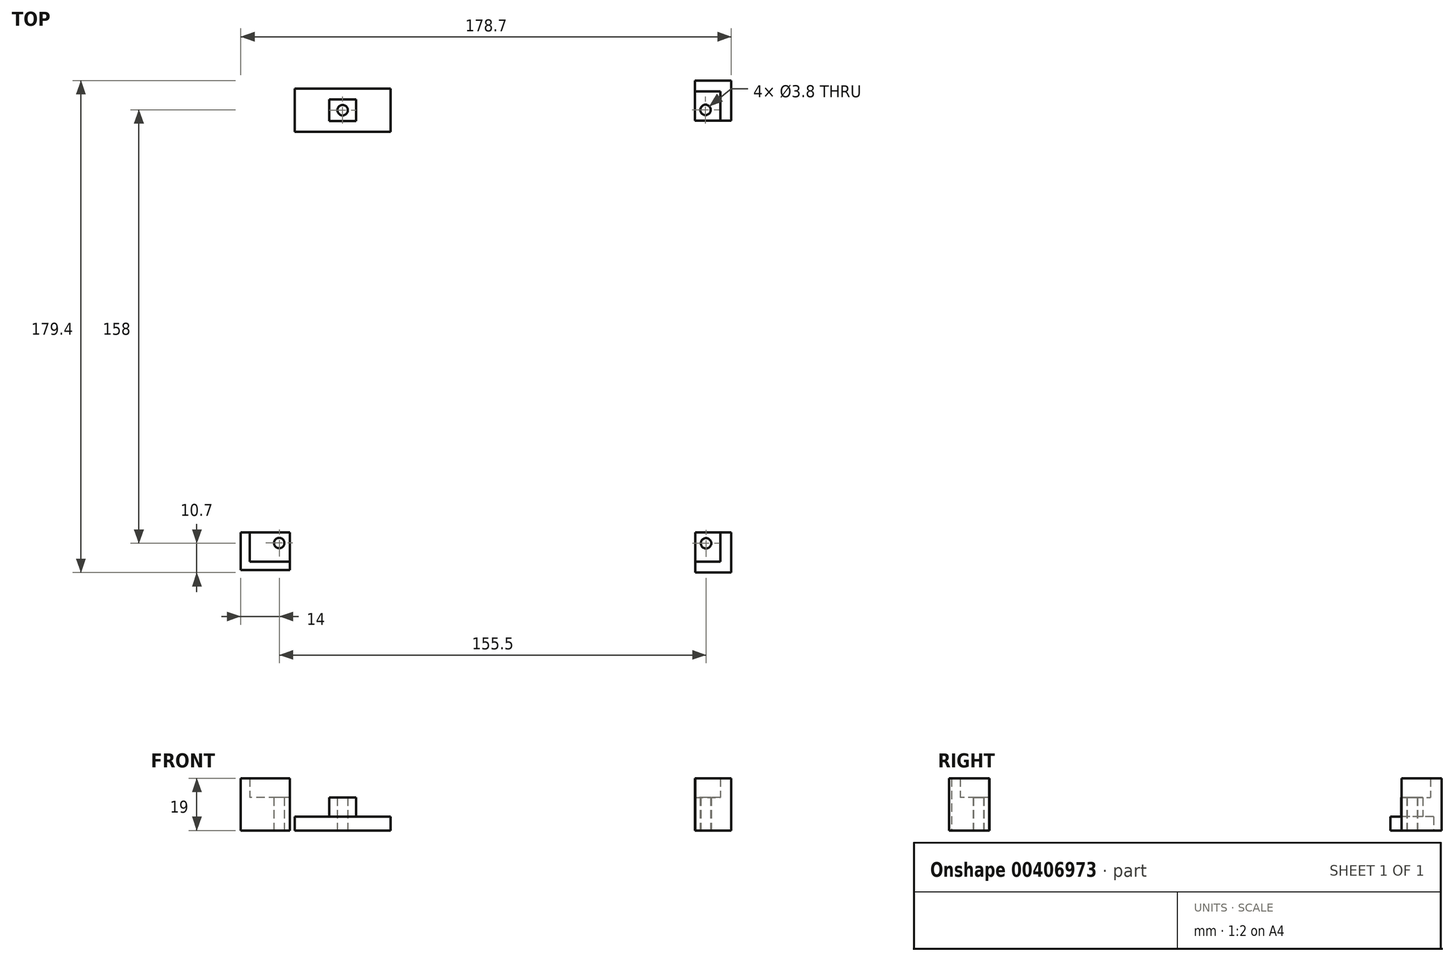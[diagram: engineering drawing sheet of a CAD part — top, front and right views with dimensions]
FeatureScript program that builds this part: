
annotation { "Feature Type Name" : "Feature", "Feature Type Description" : "" }
export const myFeature = defineFeature(function(context is Context, id is Id, definition is map)
    precondition{}
    {
        {
            var Q0;
            Q0=qCreatedBy(makeId("Top.planeOp"),FACE);
            var sketch = newSketch(context, id + "F0", { "sketchPlane" : qUnion([Q0])});
            skLineSegment(sketch, "E0.bottom", {"start": v(10, 10) * mm, "end": v(180, 10) * mm});
            skLineSegment(sketch, "E0.top", {"start": v(10, 180) * mm, "end": v(180, 180) * mm});
            skLineSegment(sketch, "E0.left", {"start": v(10, 10) * mm, "end": v(10, 180) * mm});
            skLineSegment(sketch, "E0.right", {"start": v(180, 10) * mm, "end": v(180, 180) * mm});
            skSolve(sketch);
        }
        {
            var Q0;
            Q0=qCreatedBy(makeId("Top.planeOp"),FACE);
            var sketch = newSketch(context, id + "F1", { "sketchPlane" : qUnion([Q0])});
            skCircle(sketch, "E1", {"center": v(175.5, 16) * mm, "radius": 1.5 * mm});
            skPoint(sketch, "E2", {"position": v(174, 16) * mm});
            skPoint(sketch, "E3", {"position": v(177, 16) * mm});
            skPoint(sketch, "E4", {"position": v(175.5, 14.5) * mm});
            skCircle(sketch, "E5", {"center": v(20, 16.1) * mm, "radius": 1.5 * mm});
            skPoint(sketch, "E6", {"position": v(18.5, 16.1) * mm});
            skPoint(sketch, "E7", {"position": v(20, 14.6) * mm});
            skCircle(sketch, "E8", {"center": v(43.1, 173.9) * mm, "radius": 1.5 * mm});
            skPoint(sketch, "E9", {"position": v(41.6, 173.9) * mm});
            skPoint(sketch, "E10", {"position": v(43.1, 175.4) * mm});
            skCircle(sketch, "E11", {"center": v(175.3, 174) * mm, "radius": 1.5 * mm});
            skPoint(sketch, "E12", {"position": v(175.3, 175.5) * mm});
            skPoint(sketch, "E13", {"position": v(176.8, 174) * mm});
            skSolve(sketch);
        }
        {
            var Q0;
            Q0=qCreatedBy(makeId("Top.planeOp"),FACE);
            var sketch = newSketch(context, id + "F2", { "sketchPlane" : qUnion([Q0])});
            skCircle(sketch, "E14.0", {"center": v(20, 16.1) * mm, "radius": 1.9 * mm});
            skCircle(sketch, "E15.0", {"center": v(175.5, 16) * mm, "radius": 1.9 * mm});
            skCircle(sketch, "E16.0", {"center": v(175.3, 174) * mm, "radius": 1.9 * mm});
            skCircle(sketch, "E17.0", {"center": v(43.1, 173.9) * mm, "radius": 1.9 * mm});
            skLineSegment(sketch, "E18.bottom", {"start": v(23.9, 20) * mm, "end": v(16.1, 20) * mm});
            skLineSegment(sketch, "E18.top", {"start": v(23.9, 12.2) * mm, "end": v(16.1, 12.2) * mm, "construction": true});
            skLineSegment(sketch, "E18.left", {"start": v(23.9, 20) * mm, "end": v(23.9, 12.2) * mm});
            skLineSegment(sketch, "E18.right", {"start": v(16.1, 20) * mm, "end": v(16.1, 12.2) * mm});
            skLineSegment(sketch, "E19.bottom", {"start": v(23.9, 20) * mm, "end": v(6, 20) * mm});
            skLineSegment(sketch, "E19.top", {"start": v(23.9, 6.2) * mm, "end": v(6, 6.2) * mm});
            skLineSegment(sketch, "E19.left", {"start": v(23.9, 20) * mm, "end": v(23.9, 6.2) * mm});
            skLineSegment(sketch, "E19.right", {"start": v(6, 20) * mm, "end": v(6, 6.2) * mm});
            skLineSegment(sketch, "E20.bottom", {"start": v(179.4, 19.9) * mm, "end": v(171.6, 19.9) * mm});
            skLineSegment(sketch, "E20.top", {"start": v(179.4, 12.1) * mm, "end": v(171.6, 12.1) * mm, "construction": true});
            skLineSegment(sketch, "E20.left", {"start": v(179.4, 19.9) * mm, "end": v(179.4, 12.1) * mm});
            skLineSegment(sketch, "E20.right", {"start": v(171.6, 19.9) * mm, "end": v(171.6, 12.1) * mm});
            skLineSegment(sketch, "E21.bottom", {"start": v(171.6, 19.9) * mm, "end": v(184.7, 19.9) * mm});
            skLineSegment(sketch, "E21.top", {"start": v(171.6, 5.3) * mm, "end": v(184.7, 5.3) * mm});
            skLineSegment(sketch, "E21.left", {"start": v(171.6, 19.9) * mm, "end": v(171.6, 5.3) * mm});
            skLineSegment(sketch, "E21.right", {"start": v(184.7, 19.9) * mm, "end": v(184.7, 5.3) * mm});
            skLineSegment(sketch, "E22.bottom", {"start": v(179.2, 177.9) * mm, "end": v(171.4, 177.9) * mm});
            skLineSegment(sketch, "E22.top", {"start": v(179.2, 170.1) * mm, "end": v(171.4, 170.1) * mm});
            skLineSegment(sketch, "E22.left", {"start": v(179.2, 177.9) * mm, "end": v(179.2, 170.1) * mm, "construction": true});
            skLineSegment(sketch, "E22.right", {"start": v(171.4, 177.9) * mm, "end": v(171.4, 170.1) * mm});
            skLineSegment(sketch, "E23.bottom", {"start": v(48, 177.8) * mm, "end": v(38.2, 177.8) * mm});
            skLineSegment(sketch, "E23.top", {"start": v(48, 170) * mm, "end": v(38.2, 170) * mm});
            skLineSegment(sketch, "E23.left", {"start": v(48, 177.8) * mm, "end": v(48, 170) * mm});
            skLineSegment(sketch, "E23.right", {"start": v(38.2, 177.8) * mm, "end": v(38.2, 170) * mm});
            skLineSegment(sketch, "E24.bottom", {"start": v(60.6, 181.8) * mm, "end": v(25.6, 181.8) * mm});
            skLineSegment(sketch, "E24.top", {"start": v(60.6, 166) * mm, "end": v(25.6, 166) * mm});
            skLineSegment(sketch, "E24.left", {"start": v(60.6, 181.8) * mm, "end": v(60.6, 166) * mm});
            skLineSegment(sketch, "E24.right", {"start": v(25.6, 181.8) * mm, "end": v(25.6, 166) * mm});
            skLineSegment(sketch, "E25.bottom", {"start": v(23.9, 20) * mm, "end": v(9.3, 20) * mm});
            skLineSegment(sketch, "E25.top", {"start": v(23.9, 9.3) * mm, "end": v(9.3, 9.3) * mm});
            skLineSegment(sketch, "E25.left", {"start": v(23.9, 20) * mm, "end": v(23.9, 9.3) * mm});
            skLineSegment(sketch, "E25.right", {"start": v(9.3, 20) * mm, "end": v(9.3, 9.3) * mm});
            skLineSegment(sketch, "E26.bottom", {"start": v(171.6, 19.9) * mm, "end": v(180.7, 19.9) * mm});
            skLineSegment(sketch, "E26.top", {"start": v(171.6, 9.3) * mm, "end": v(180.7, 9.3) * mm});
            skLineSegment(sketch, "E26.left", {"start": v(171.6, 19.9) * mm, "end": v(171.6, 9.3) * mm});
            skLineSegment(sketch, "E26.right", {"start": v(180.7, 19.9) * mm, "end": v(180.7, 9.3) * mm});
            skLineSegment(sketch, "E27.bottom", {"start": v(171.4, 170.1) * mm, "end": v(180.7, 170.1) * mm});
            skLineSegment(sketch, "E27.top", {"start": v(171.4, 180.7) * mm, "end": v(180.7, 180.7) * mm});
            skLineSegment(sketch, "E27.left", {"start": v(171.4, 170.1) * mm, "end": v(171.4, 180.7) * mm});
            skLineSegment(sketch, "E27.right", {"start": v(180.7, 170.1) * mm, "end": v(180.7, 180.7) * mm});
            skLineSegment(sketch, "E28.bottom", {"start": v(171.4, 170.1) * mm, "end": v(184.7, 170.1) * mm});
            skLineSegment(sketch, "E28.top", {"start": v(171.4, 184.7) * mm, "end": v(184.7, 184.7) * mm});
            skLineSegment(sketch, "E28.left", {"start": v(171.4, 170.1) * mm, "end": v(171.4, 184.7) * mm});
            skLineSegment(sketch, "E28.right", {"start": v(184.7, 170.1) * mm, "end": v(184.7, 184.7) * mm});
            skSolve(sketch);
        }
        {
            var Q0;
            Q0=qCreatedBy(makeId("Front.planeOp"),FACE);
            var sketch = newSketch(context, id + "F3", { "sketchPlane" : qUnion([Q0])});
            skLineSegment(sketch, "E29", {"start": v(-119.23, 0) * mm, "end": v(-119.23, 12) * mm, "construction": true});
            skLineSegment(sketch, "E30", {"start": v(-119.23, 12) * mm, "end": v(-119.23, 19) * mm, "construction": true});
            skLineSegment(sketch, "E31", {"start": v(-171.62, 12) * mm, "end": v(-171.62, 15) * mm, "construction": true});
            skSolve(sketch);
        }
        {
            var Q0;
            Q0=makeQuery(id+"F0.imprint","IMPRINT",FACE,{"disambiguationData":[TD([[makeQuery(id+"F0.imprint","IMPRINT",EDGE,{"derivedFrom":sQuery(id+"F0.wireOp",EDGE,"E0.bottom")}),1.0]])]});
            var Q1;
            Q1=sQuery(id+"F3.wireOp",VERTEX,"E31.end");
            var Q2;
            Q2=sQuery(id+"F3.wireOp",VERTEX,"E31.start");
            extrude(context, id + "F4", {"entities" : qUnion([Q0]), "endBound" : BoundingType.UP_TO_VERTEX, "endBoundEntityVertex" : qUnion([Q1]), "depth" : 25 * mm, "hasSecondDirection" : true, "secondDirectionBound" : SecondDirectionBoundingType.UP_TO_VERTEX, "secondDirectionOppositeDirection" : false, "secondDirectionBoundEntityVertex" : qUnion([Q2]), "secondDirectionDepth" : 25 * mm});
        }
        {
            var Q0;
            Q0=makeQuery(id+"F1.imprint","IMPRINT",FACE,{"disambiguationData":[TD([[makeQuery(id+"F1.imprint","IMPRINT",EDGE,{"derivedFrom":sQuery(id+"F1.wireOp",EDGE,"E8")}),1.0]])]});
            var Q1;
            Q1=makeQuery(id+"F1.imprint","IMPRINT",FACE,{"disambiguationData":[TD([[makeQuery(id+"F1.imprint","IMPRINT",EDGE,{"derivedFrom":sQuery(id+"F1.wireOp",EDGE,"E11")}),1.0]])]});
            var Q2;
            Q2=makeQuery(id+"F1.imprint","IMPRINT",FACE,{"disambiguationData":[TD([[makeQuery(id+"F1.imprint","IMPRINT",EDGE,{"derivedFrom":sQuery(id+"F1.wireOp",EDGE,"E5")}),1.0]])]});
            var Q3;
            Q3=makeQuery(id+"F1.imprint","IMPRINT",FACE,{"disambiguationData":[TD([[makeQuery(id+"F1.imprint","IMPRINT",EDGE,{"derivedFrom":sQuery(id+"F1.wireOp",EDGE,"E1")}),1.0]])]});
            var Q4;
            Q4=sQuery(id+"F1.wireOp",EDGE,"E5");
            var Q5;
            Q5=sQuery(id+"F1.wireOp",EDGE,"E1");
            var Q6;
            Q6=sQuery(id+"F1.wireOp",EDGE,"E11");
            var Q7;
            Q7=sQuery(id+"F1.wireOp",EDGE,"E8");
            extrude(context, id + "F5", {"entities" : qUnion([Q0, Q1, Q2, Q3]), "operationType" : NewBodyOperationType.REMOVE, "surfaceEntities" : qUnion([Q4, Q5, Q6, Q7]), "depth" : 25 * mm});
        }
        {
            var Q0;
            Q0=makeQuery(id+"F2.imprint","IMPRINT",FACE,{"disambiguationData":[TD([[makeQuery(id+"F2.imprint","IMPRINT",EDGE,{"derivedFrom":sQuery(id+"F2.wireOp",EDGE,"E14.0")}),-1.0]])]});
            var Q1;
            Q1=makeQuery(id+"F2.imprint","IMPRINT",FACE,{"disambiguationData":[TD([[makeQuery(id+"F2.imprint","IMPRINT",EDGE,{"derivedFrom":sQuery(id+"F2.wireOp",EDGE,"E15.0")}),-1.0]])]});
            var Q2;
            Q2=makeQuery(id+"F2.imprint","IMPRINT",FACE,{"disambiguationData":[TD([[makeQuery(id+"F2.imprint","IMPRINT",EDGE,{"derivedFrom":sQuery(id+"F2.wireOp",EDGE,"E16.0")}),-1.0]])]});
            var Q3;
            Q3=makeQuery(id+"F2.imprint","IMPRINT",FACE,{"disambiguationData":[TD([[makeQuery(id+"F2.imprint","IMPRINT",EDGE,{"derivedFrom":sQuery(id+"F2.wireOp",EDGE,"E17.0")}),-1.0]])]});
            var Q4;
            Q4=sQuery(id+"F3.wireOp",VERTEX,"E30.start");
            extrude(context, id + "F6", {"entities" : qUnion([Q0, Q1, Q2, Q3]), "endBound" : BoundingType.UP_TO_VERTEX, "endBoundEntityVertex" : qUnion([Q4]), "depth" : 25 * mm});
        }
        {
            var Q0;
            Q0=makeQuery(id+"F2.imprint","IMPRINT",FACE,{"disambiguationData":[TD([[makeQuery(id+"F2.imprint","IMPRINT",EDGE,{"derivedFrom":sQuery(id+"F2.wireOp",EDGE,"E19.bottom")}),1.0]])]});
            var Q1;
            Q1=makeQuery(id+"F2.imprint","IMPRINT",FACE,{"disambiguationData":[TD([[makeQuery(id+"F2.imprint","IMPRINT",EDGE,{"derivedFrom":sQuery(id+"F2.wireOp",EDGE,"E21.bottom")}),-1.0]])]});
            var Q2;
            {var subQ4=sQuery(id+"F2.wireOp",EDGE,"E27.top");Q2=makeQuery(id+"F2.imprint","IMPRINT",FACE,{"disambiguationData":[TD([[makeQuery(id+"F2.imprint","IMPRINT",EDGE,{"derivedFrom":subQ4}),1.0]])]});}
            var Q3;
            Q3=sQuery(id+"F3.wireOp",VERTEX,"E30.end");
            extrude(context, id + "F7", {"entities" : qUnion([Q0, Q1, Q2]), "operationType" : NewBodyOperationType.ADD, "endBound" : BoundingType.UP_TO_VERTEX, "endBoundEntityVertex" : qUnion([Q3]), "depth" : 12 * mm});
        }
        {
            var Q0;
            Q0=makeQuery(id+"F2.imprint","IMPRINT",FACE,{"disambiguationData":[TD([[makeQuery(id+"F2.imprint","IMPRINT",EDGE,{"derivedFrom":sQuery(id+"F2.wireOp",EDGE,"E23.bottom")}),-1.0]])]});
            extrude(context, id + "F8", {"entities" : qUnion([Q0]), "operationType" : NewBodyOperationType.ADD, "depth" : 5 * mm});
        }
        {
            var Q0;
            Q0=makeQuery(id+"F4.opExtrude","SWEPT_BODY",BODY,{"disambiguationData":[OSD([sQuery(id+"F0.wireOp",EDGE,"E0.bottom"),sQuery(id+"F0.wireOp",EDGE,"E0.top"),sQuery(id+"F0.wireOp",EDGE,"E0.left"),sQuery(id+"F0.wireOp",EDGE,"E0.right")])]});
            deleteBodies(context, id + "F9", {"entities" : qUnion([Q0])});
        }
    });
